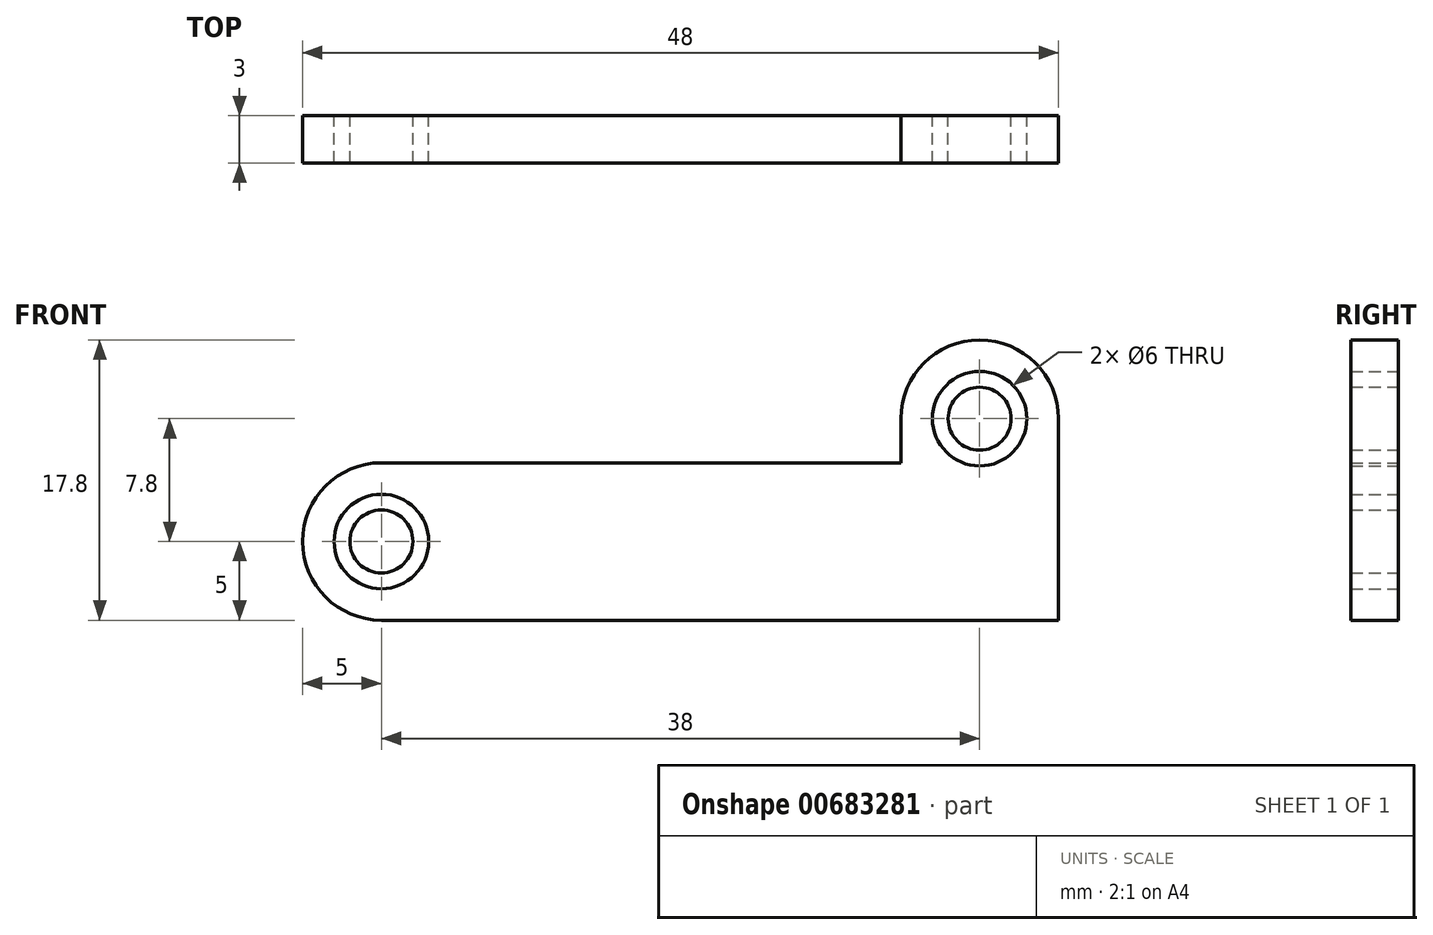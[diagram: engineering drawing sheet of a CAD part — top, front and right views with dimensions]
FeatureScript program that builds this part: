
annotation { "Feature Type Name" : "Feature", "Feature Type Description" : "" }
export const myFeature = defineFeature(function(context is Context, id is Id, definition is map)
    precondition{}
    {
        {
            var Q0;
            Q0=qCreatedBy(makeId("Front.planeOp"),FACE);
            var sketch = newSketch(context, id + "F0", { "sketchPlane" : qUnion([Q0])});
            skArc(sketch, "E0", {"start": v(5, 7.8) * mm, "mid": v(0, 12.8) * mm, "end": v(-5, 7.8) * mm});
            skArc(sketch, "E1", {"start": v(-38, 5) * mm, "mid": v(-43, 0) * mm, "end": v(-38, -5) * mm});
            skCircle(sketch, "E2", {"center": v(0, 7.8) * mm, "radius": 3 * mm});
            skCircle(sketch, "E3", {"center": v(0, 7.8) * mm, "radius": 2 * mm});
            skCircle(sketch, "E4", {"center": v(-38, 0) * mm, "radius": 3 * mm});
            skCircle(sketch, "E5", {"center": v(-38, 0) * mm, "radius": 2 * mm});
            skLineSegment(sketch, "E6", {"start": v(-5, 7.8) * mm, "end": v(-5, 5) * mm});
            skLineSegment(sketch, "E7", {"start": v(5, 7.8) * mm, "end": v(5, -5) * mm});
            skLineSegment(sketch, "E8", {"start": v(-38, 5) * mm, "end": v(-5, 5) * mm});
            skLineSegment(sketch, "E9", {"start": v(-38, -5) * mm, "end": v(5, -5) * mm});
            skSolve(sketch);
        }
        {
            var Q0;
            Q0 = qSketchRegion(id + "F0", true);
            var Q1;
            Q1=makeQuery(id+"F0.imprint","IMPRINT",FACE,{"disambiguationData":[TD([[makeQuery(id+"F0.imprint","IMPRINT",EDGE,{"derivedFrom":sQuery(id+"F0.wireOp",EDGE,"E5")}),1.0]])]});
            var Q2;
            Q2=makeQuery(id+"F0.imprint","IMPRINT",FACE,{"disambiguationData":[TD([[makeQuery(id+"F0.imprint","IMPRINT",EDGE,{"derivedFrom":sQuery(id+"F0.wireOp",EDGE,"E3")}),1.0]])]});
            extrude(context, id + "F1", {"entities" : qUnion([Q0, Q1, Q2]), "depth" : 3 * mm, "offsetDistance" : 25 * mm});
        }
    });
